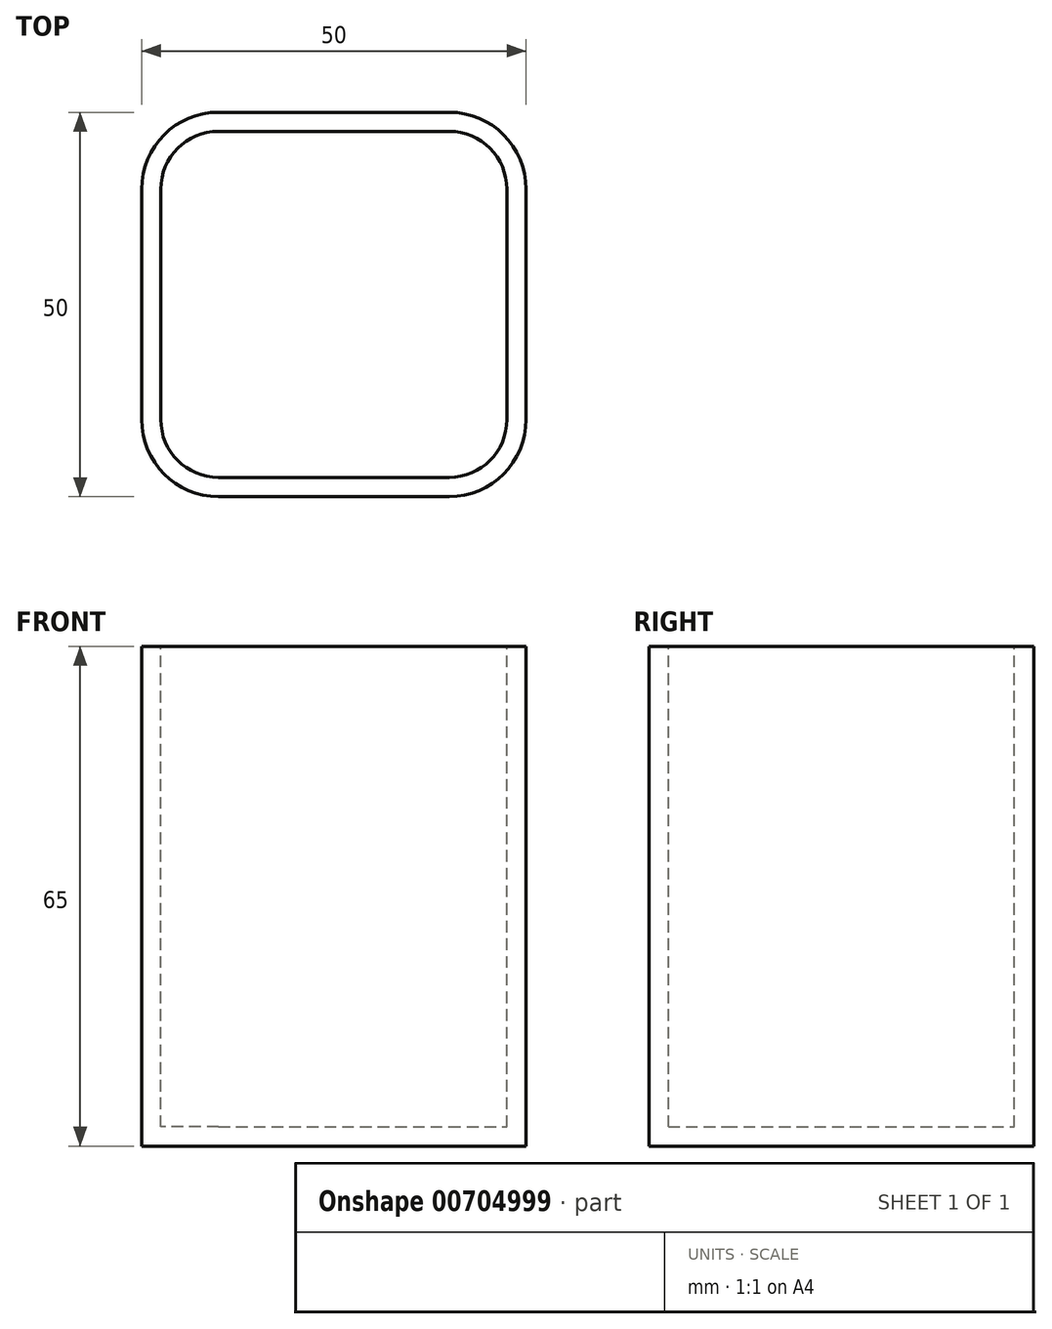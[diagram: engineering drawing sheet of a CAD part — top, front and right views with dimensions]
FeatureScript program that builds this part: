
annotation { "Feature Type Name" : "Feature", "Feature Type Description" : "" }
export const myFeature = defineFeature(function(context is Context, id is Id, definition is map)
    precondition{}
    {
        {
            var Q0;
            Q0=qCreatedBy(makeId("Top.planeOp"),FACE);
            var sketch = newSketch(context, id + "F0", { "sketchPlane" : qUnion([Q0])});
            skLineSegment(sketch, "E0.bottom", {"start": v(-25, -25) * mm, "end": v(25, -25) * mm});
            skLineSegment(sketch, "E0.top", {"start": v(-25, 25) * mm, "end": v(25, 25) * mm});
            skLineSegment(sketch, "E0.left", {"start": v(-25, -25) * mm, "end": v(-25, 25) * mm});
            skLineSegment(sketch, "E0.right", {"start": v(25, -25) * mm, "end": v(25, 25) * mm});
            skPoint(sketch, "E0.middle", {"position": v(0, 0) * mm});
            skSolve(sketch);
        }
        {
            var Q0;
            Q0=makeQuery(id+"F0.imprint","IMPRINT",FACE,{"disambiguationData":[TD([[makeQuery(id+"F0.imprint","IMPRINT",EDGE,{"derivedFrom":sQuery(id+"F0.wireOp",EDGE,"E0.bottom")}),1.0]])]});
            extrude(context, id + "F1", {"entities" : qUnion([Q0]), "depth" : 50 * mm, "offsetDistance" : 25 * mm});
        }
        {
            var Q0;
            Q0=makeQuery(id+"F1.opExtrude","SWEPT_EDGE",EDGE,{"disambiguationData":[OSD([sQuery(id+"F0.wireOp",EDGE,"E0.bottom"),sQuery(id+"F0.wireOp",EDGE,"E0.left")])]});
            var Q1;
            Q1=makeQuery(id+"F1.opExtrude","SWEPT_EDGE",EDGE,{"disambiguationData":[OSD([sQuery(id+"F0.wireOp",EDGE,"E0.top"),sQuery(id+"F0.wireOp",EDGE,"E0.left")])]});
            var Q2;
            Q2=makeQuery(id+"F1.opExtrude","SWEPT_EDGE",EDGE,{"disambiguationData":[OSD([sQuery(id+"F0.wireOp",EDGE,"E0.top"),sQuery(id+"F0.wireOp",EDGE,"E0.right")])]});
            var Q3;
            Q3=makeQuery(id+"F1.opExtrude","SWEPT_EDGE",EDGE,{"disambiguationData":[OSD([sQuery(id+"F0.wireOp",EDGE,"E0.bottom"),sQuery(id+"F0.wireOp",EDGE,"E0.right")])]});
            fillet(context, id + "F2", {"entities" : qUnion([Q0, Q1, Q2, Q3]), "radius" : 10 * mm, "tangentPropagation" : true, "allowEdgeOverflow" : false});
        }
        {
            var Q0;
            Q0=makeQuery(id+"F1.opExtrude","CAP_FACE",FACE,{"disambiguationData":[OSD([sQuery(id+"F0.wireOp",EDGE,"E0.bottom"),sQuery(id+"F0.wireOp",EDGE,"E0.top"),sQuery(id+"F0.wireOp",EDGE,"E0.left"),sQuery(id+"F0.wireOp",EDGE,"E0.right")])],"isStart":true});
            extrude(context, id + "F3", {"entities" : qUnion([Q0]), "operationType" : NewBodyOperationType.ADD, "depth" : 15 * mm, "offsetDistance" : 25 * mm});
        }
        {
            var Q0;
            Q0=makeQuery(id+"F1.opExtrude","CAP_FACE",FACE,{"disambiguationData":[OSD([sQuery(id+"F0.wireOp",EDGE,"E0.bottom"),sQuery(id+"F0.wireOp",EDGE,"E0.top"),sQuery(id+"F0.wireOp",EDGE,"E0.left"),sQuery(id+"F0.wireOp",EDGE,"E0.right")])],"isStart":false});
            shell(context, id + "F4", {"entities" : qUnion([Q0]), "thickness" : 2.5 * mm});
        }
    });
